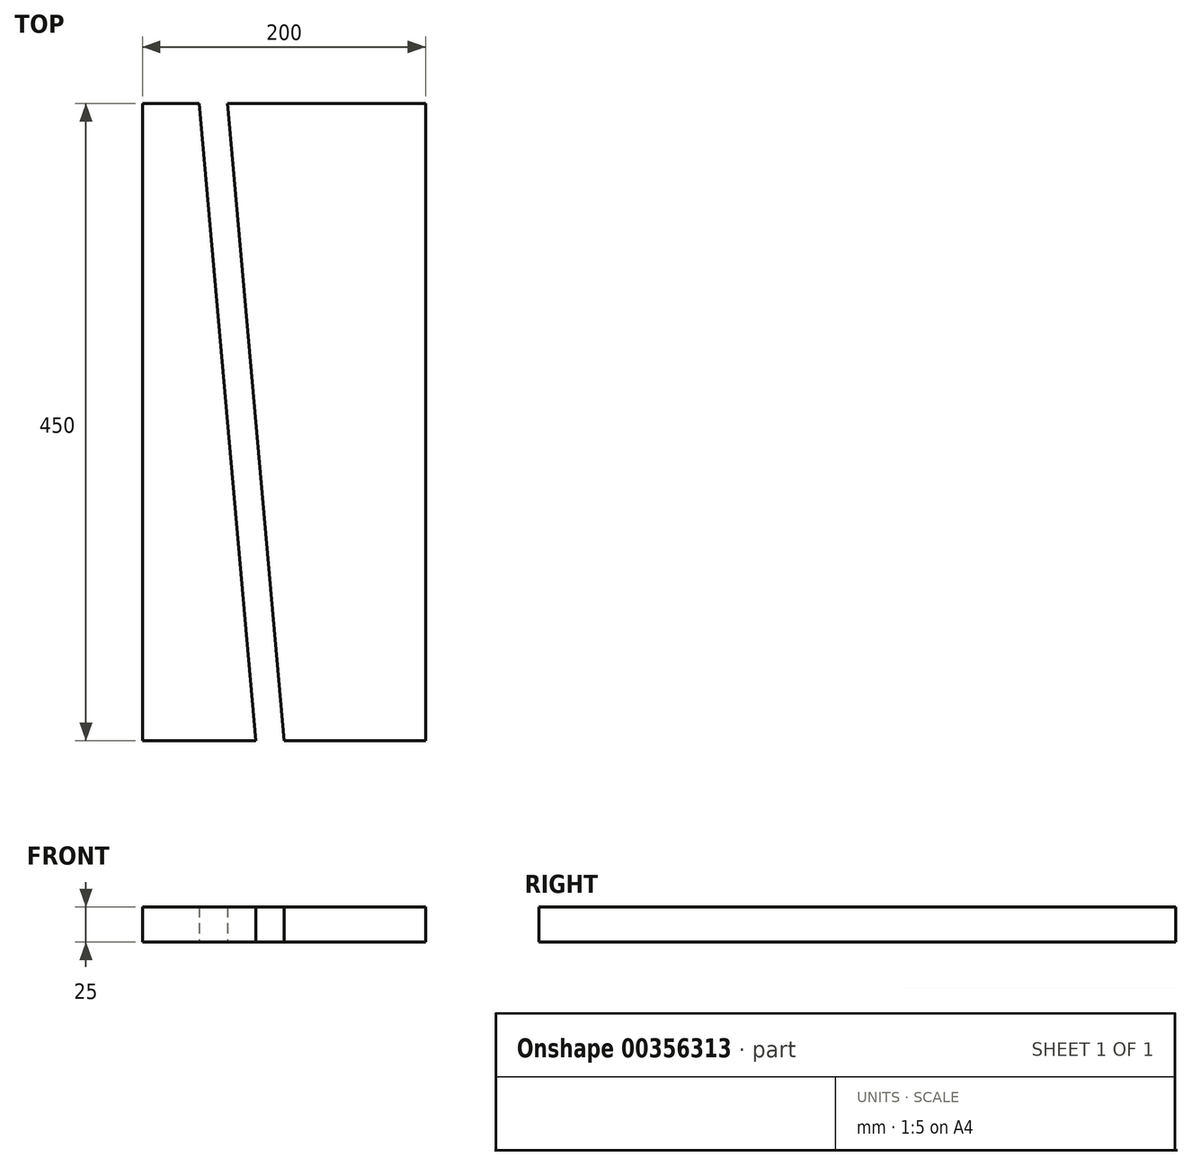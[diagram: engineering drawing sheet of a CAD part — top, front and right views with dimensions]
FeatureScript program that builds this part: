
annotation { "Feature Type Name" : "Feature", "Feature Type Description" : "" }
export const myFeature = defineFeature(function(context is Context, id is Id, definition is map)
    precondition{}
    {
        {
            var Q0;
            Q0=qCreatedBy(makeId("Top.planeOp"),FACE);
            var sketch = newSketch(context, id + "F0", { "sketchPlane" : qUnion([Q0])});
            skLineSegment(sketch, "E0", {"start": v(0, 0) * mm, "end": v(80, 0) * mm});
            skLineSegment(sketch, "E1", {"start": v(80, 0) * mm, "end": v(40, 450) * mm});
            skLineSegment(sketch, "E2", {"start": v(40, 450) * mm, "end": v(0, 450) * mm});
            skLineSegment(sketch, "E3", {"start": v(0, 450) * mm, "end": v(0, 0) * mm});
            skLineSegment(sketch, "E4", {"start": v(80, 0) * mm, "end": v(100, 0) * mm, "construction": true});
            skLineSegment(sketch, "E5", {"start": v(100, 0) * mm, "end": v(200, 0) * mm});
            skLineSegment(sketch, "E6", {"start": v(200, 0) * mm, "end": v(200, 450) * mm});
            skLineSegment(sketch, "E7", {"start": v(200, 450) * mm, "end": v(60, 450) * mm});
            skLineSegment(sketch, "E8", {"start": v(60, 450) * mm, "end": v(100, 0) * mm});
            skSolve(sketch);
        }
        {
            var Q0;
            Q0=makeQuery(id+"F0.imprint","IMPRINT",FACE,{"disambiguationData":[TD([[makeQuery(id+"F0.imprint","IMPRINT",EDGE,{"derivedFrom":sQuery(id+"F0.wireOp",EDGE,"E0")}),1.0]])]});
            var Q1;
            Q1=makeQuery(id+"F0.imprint","IMPRINT",FACE,{"disambiguationData":[TD([[makeQuery(id+"F0.imprint","IMPRINT",EDGE,{"derivedFrom":sQuery(id+"F0.wireOp",EDGE,"E5")}),1.0]])]});
            extrude(context, id + "F1", {"entities" : qUnion([Q0, Q1]), "depth" : 25 * mm});
        }
    });
